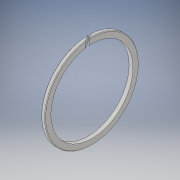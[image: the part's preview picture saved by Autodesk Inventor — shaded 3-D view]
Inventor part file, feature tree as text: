
AUTODESK INVENTOR PART (.ipt)
format: ipt  version: 2018 (Build 220112000, 112)  size: 151,552 bytes
history: native  units: mm
features: extrude x2, sketch x2, fillet x1, projected_geometry x1
ambient origin geometry x8: Origin, YZ Plane, XZ Plane, XY Plane, X Axis, Y Axis, Z Axis, Center Point
bodies: Solid1 (feature_tree)
feature tree (6):
  extrude  "Extrusion1"  Depth=21.0mm
  extrude  "Extrusion2"  Depth=0.15mm
  fillet  "Fillet1"  [1 undecoded]
  sketch  "Sketch1"  dims[d0=24.0mm d1=21.0mm]
  sketch  "Sketch2"  dims[d2=1.0mm d3=0.0mm d4=12.73mm d5=30.0deg d6=1.0mm d7=17.0mm d8=0.0mm d9=0.15mm]
  projected_geometry  "Project Cut Edges1"
note: 1 required parameter value undecoded (feature->parameter linkage not recoverable at this tier; creation-order binding heuristic only, values carry confidence <= 0.55)
